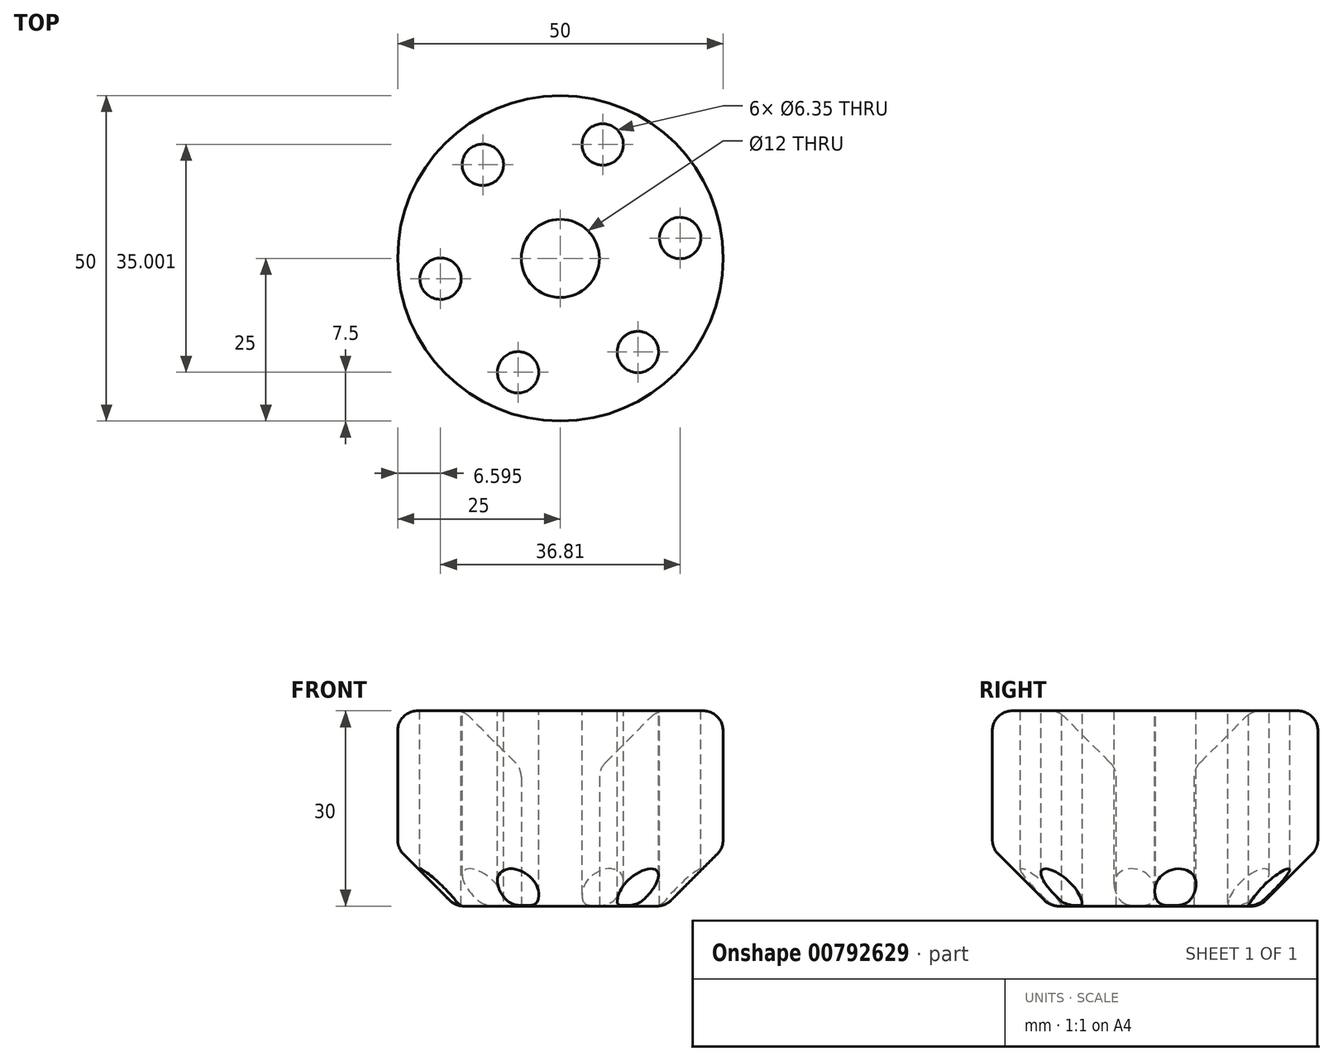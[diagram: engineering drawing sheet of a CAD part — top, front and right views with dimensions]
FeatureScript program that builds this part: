
annotation { "Feature Type Name" : "Feature", "Feature Type Description" : "" }
export const myFeature = defineFeature(function(context is Context, id is Id, definition is map)
    precondition{}
    {
        {
            var Q0;
            Q0=qCreatedBy(makeId("Top.planeOp"),FACE);
            var sketch = newSketch(context, id + "F0", { "sketchPlane" : qUnion([Q0])});
            skCircle(sketch, "E0", {"center": v(0, 0) * mm, "radius": 25 * mm});
            skCircle(sketch, "E1", {"center": v(0, 0) * mm, "radius": 6 * mm});
            skSolve(sketch);
        }
        {
            var Q0;
            Q0=makeQuery(id+"F0.imprint","IMPRINT",FACE,{"disambiguationData":[TD([[makeQuery(id+"F0.imprint","IMPRINT",EDGE,{"derivedFrom":sQuery(id+"F0.wireOp",EDGE,"E0")}),1.0]])]});
            extrude(context, id + "F1", {"entities" : qUnion([Q0]), "depth" : 30 * mm, "offsetDistance" : 25.4 * mm});
        }
        {
            var Q0;
            Q0=makeQuery(id+"F1.opExtrude","CAP_EDGE",EDGE,{"disambiguationData":[OSD([sQuery(id+"F0.wireOp",EDGE,"E1")])],"isStart":false});
            var Q1;
            Q1=makeQuery(id+"F1.opExtrude","CAP_EDGE",EDGE,{"disambiguationData":[OSD([sQuery(id+"F0.wireOp",EDGE,"E0")])],"isStart":true});
            chamfer(context, id + "F2", {"entities" : qUnion([Q0, Q1]), "width" : 8.9 * mm, "tangentPropagation" : true});
        }
        {
            var Q0;
            Q0=makeQuery(id+"F1.opExtrude","CAP_EDGE",EDGE,{"disambiguationData":[OSD([sQuery(id+"F0.wireOp",EDGE,"E0")])],"isStart":false});
            var Q1;
            {var subQ0=sQuery(id+"F0.wireOp",EDGE,"E1");Q1=makeQuery(id+"F2.opChamfer","BLEND_EDGE",EDGE,{"blendedFrom":[makeQuery(id+"F1.opExtrude","CAP_EDGE",EDGE,{"disambiguationData":[OSD([subQ0])],"isStart":false}),makeQuery(id+"F1.opExtrude","CAP_FACE",FACE,{"disambiguationData":[OSD([sQuery(id+"F0.wireOp",EDGE,"E0"),subQ0])],"isStart":false})],"blendedInto":[makeQuery(id+"F1.opExtrude","CAP_FACE",FACE,{"disambiguationData":[OSD([sQuery(id+"F0.wireOp",EDGE,"E0"),subQ0])],"isStart":false})]});}
            var Q2;
            {var subQ0=sQuery(id+"F0.wireOp",EDGE,"E0");Q2=makeQuery(id+"F2.opChamfer","BLEND_EDGE",EDGE,{"blendedFrom":[makeQuery(id+"F1.opExtrude","CAP_EDGE",EDGE,{"disambiguationData":[OSD([subQ0])],"isStart":true}),makeQuery(id+"F1.opExtrude","SWEPT_FACE",FACE,{"disambiguationData":[OSD([subQ0])]})],"blendedInto":[makeQuery(id+"F1.opExtrude","SWEPT_FACE",FACE,{"disambiguationData":[OSD([subQ0])]})]});}
            var Q3;
            {var subQ0=sQuery(id+"F0.wireOp",EDGE,"E0");Q3=makeQuery(id+"F2.opChamfer","BLEND_EDGE",EDGE,{"blendedFrom":[makeQuery(id+"F1.opExtrude","CAP_EDGE",EDGE,{"disambiguationData":[OSD([subQ0])],"isStart":true}),makeQuery(id+"F1.opExtrude","CAP_FACE",FACE,{"disambiguationData":[OSD([subQ0,sQuery(id+"F0.wireOp",EDGE,"E1")])],"isStart":true})],"blendedInto":[makeQuery(id+"F1.opExtrude","CAP_FACE",FACE,{"disambiguationData":[OSD([subQ0,sQuery(id+"F0.wireOp",EDGE,"E1")])],"isStart":true})]});}
            var Q4;
            {var subQ0=sQuery(id+"F0.wireOp",EDGE,"E1");Q4=makeQuery(id+"F2.opChamfer","BLEND_EDGE",EDGE,{"blendedFrom":[makeQuery(id+"F1.opExtrude","CAP_EDGE",EDGE,{"disambiguationData":[OSD([subQ0])],"isStart":false}),makeQuery(id+"F1.opExtrude","SWEPT_FACE",FACE,{"disambiguationData":[OSD([subQ0])]})],"blendedInto":[makeQuery(id+"F1.opExtrude","SWEPT_FACE",FACE,{"disambiguationData":[OSD([subQ0])]})]});}
            fillet(context, id + "F3", {"entities" : qUnion([Q0, Q1, Q2, Q3, Q4]), "radius" : 3.08 * mm, "tangentPropagation" : true, "allowEdgeOverflow" : false});
        }
        {
            var Q0;
            Q0=makeQuery(id+"F1.opExtrude","CAP_FACE",FACE,{"disambiguationData":[OSD([sQuery(id+"F0.wireOp",EDGE,"E0"),sQuery(id+"F0.wireOp",EDGE,"E1")])],"isStart":false});
            var sketch = newSketch(context, id + "F4", { "sketchPlane" : qUnion([Q0])});
            skCircle(sketch, "E2.cCircle", {"center": v(0, 0) * mm, "radius": 16.17 * mm, "construction": true});
            skLineSegment(sketch, "E2.0", {"start": v(18.4, 3.12) * mm, "end": v(11.9, -14.38) * mm});
            skLineSegment(sketch, "E2.1", {"start": v(11.9, -14.38) * mm, "end": v(-6.5, -17.5) * mm});
            skLineSegment(sketch, "E2.2", {"start": v(-6.5, -17.5) * mm, "end": v(-18.4, -3.12) * mm});
            skLineSegment(sketch, "E2.3", {"start": v(-18.4, -3.12) * mm, "end": v(-11.9, 14.38) * mm});
            skLineSegment(sketch, "E2.4", {"start": v(-11.9, 14.38) * mm, "end": v(6.5, 17.5) * mm});
            skLineSegment(sketch, "E2.5", {"start": v(6.5, 17.5) * mm, "end": v(18.4, 3.12) * mm});
            skPoint(sketch, "E2.0.midPoint", {"position": v(15.16, -5.63) * mm});
            skSolve(sketch);
        }
        {
            var Q0;
            Q0=sQuery(id+"F4.wireOp",VERTEX,"E2.0.start");
            var Q1;
            Q1=sQuery(id+"F4.wireOp",VERTEX,"E2.4.end");
            var Q2;
            Q2=sQuery(id+"F4.wireOp",VERTEX,"E2.3.end");
            var Q3;
            Q3=sQuery(id+"F4.wireOp",VERTEX,"E2.2.end");
            var Q4;
            Q4=sQuery(id+"F4.wireOp",VERTEX,"E2.1.end");
            var Q5;
            Q5=sQuery(id+"F4.wireOp",VERTEX,"E2.0.end");
            var Q6;
            Q6=makeQuery(id+"F1.opExtrude","SWEPT_BODY",BODY,{"disambiguationData":[OSD([sQuery(id+"F0.wireOp",EDGE,"E0"),sQuery(id+"F0.wireOp",EDGE,"E1")])]});
            hole(context, id + "F5", {"style" : HoleStyle.SIMPLE, "endStyle" : HoleEndStyle.THROUGH, "holeDiameter" : 6.35 * mm, "majorDiameter" : 6.35 * mm, "isTappedThrough" : true, "tappedDepth" : 12.7 * mm, "tapClearance" : 3, "startFromSketch" : true, "locations" : qUnion([Q0, Q1, Q2, Q3, Q4, Q5]), "scope" : qUnion([Q6])});
        }
    });
